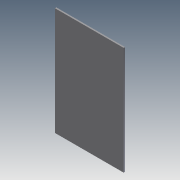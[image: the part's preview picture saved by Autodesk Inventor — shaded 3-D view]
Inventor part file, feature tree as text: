
AUTODESK INVENTOR PART (.ipt)
format: ipt  version: 2011 (Build 150239000, 239)  size: 64,000 bytes
history: native  units: in
note: dims shown in document units (in); Inventor stores cm internally (conversion verified against a paired STEP export)
features: extrude x1, sketch x1
ambient origin geometry x8: Origin, YZ Plane, XZ Plane, XY Plane, X Axis, Y Axis, Z Axis, Center Point
bodies: Solid1 (feature_tree)
feature tree (2):
  extrude  "Extrusion1"  Depth=18.97in
  sketch  "Sketch1"  dims[d0=12.07in d1=18.97in d2=0.25in d3=0.0in]
